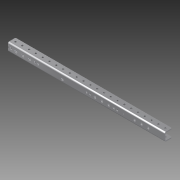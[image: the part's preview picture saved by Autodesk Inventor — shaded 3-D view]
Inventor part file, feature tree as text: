
AUTODESK INVENTOR PART (.ipt)
format: ipt  version: 2014 (Build 180170000, 170)  size: 174,080 bytes
history: native  units: in
note: dims shown in document units (in); Inventor stores cm internally (conversion verified against a paired STEP export)
features: sketch x3, extrude x2, chamfer x1, hole x1, pattern_linear x1
ambient origin geometry x8: Origin, YZ Plane, XZ Plane, XY Plane, X Axis, Y Axis, Z Axis, Center Point
bodies: Solid1 (feature_tree)
feature tree (8):
  extrude  "Extrusion1"  Depth=0.125in TaperAngle=45.0deg
  chamfer  "Chamfer1"  Distance=1.0in
  hole  "Hole1"  [1 undecoded]
  pattern_linear  "Rectangular Pattern1"  [2 undecoded]
  extrude  "Extrusion2"  [1 undecoded]
  sketch  "Sketch1"  dims[d0=23.0in d1=0.0in d2=0.125in d3=0.125in d4=45.0deg]
  sketch  "Sketch2"  dims[d5=0.5in]
  sketch  "Sketch3"  dims[d6=0.5in d7=0.264in d8=0.75in d9=0.375in d10=0.25in d11=0.5635in d12=1.0in d13=0.8108in d14=11.811in d16=1.0in d17=1.0in d18=0.0in]
note: 4 required parameter values undecoded (feature->parameter linkage not recoverable at this tier; creation-order binding heuristic only, values carry confidence <= 0.55)
